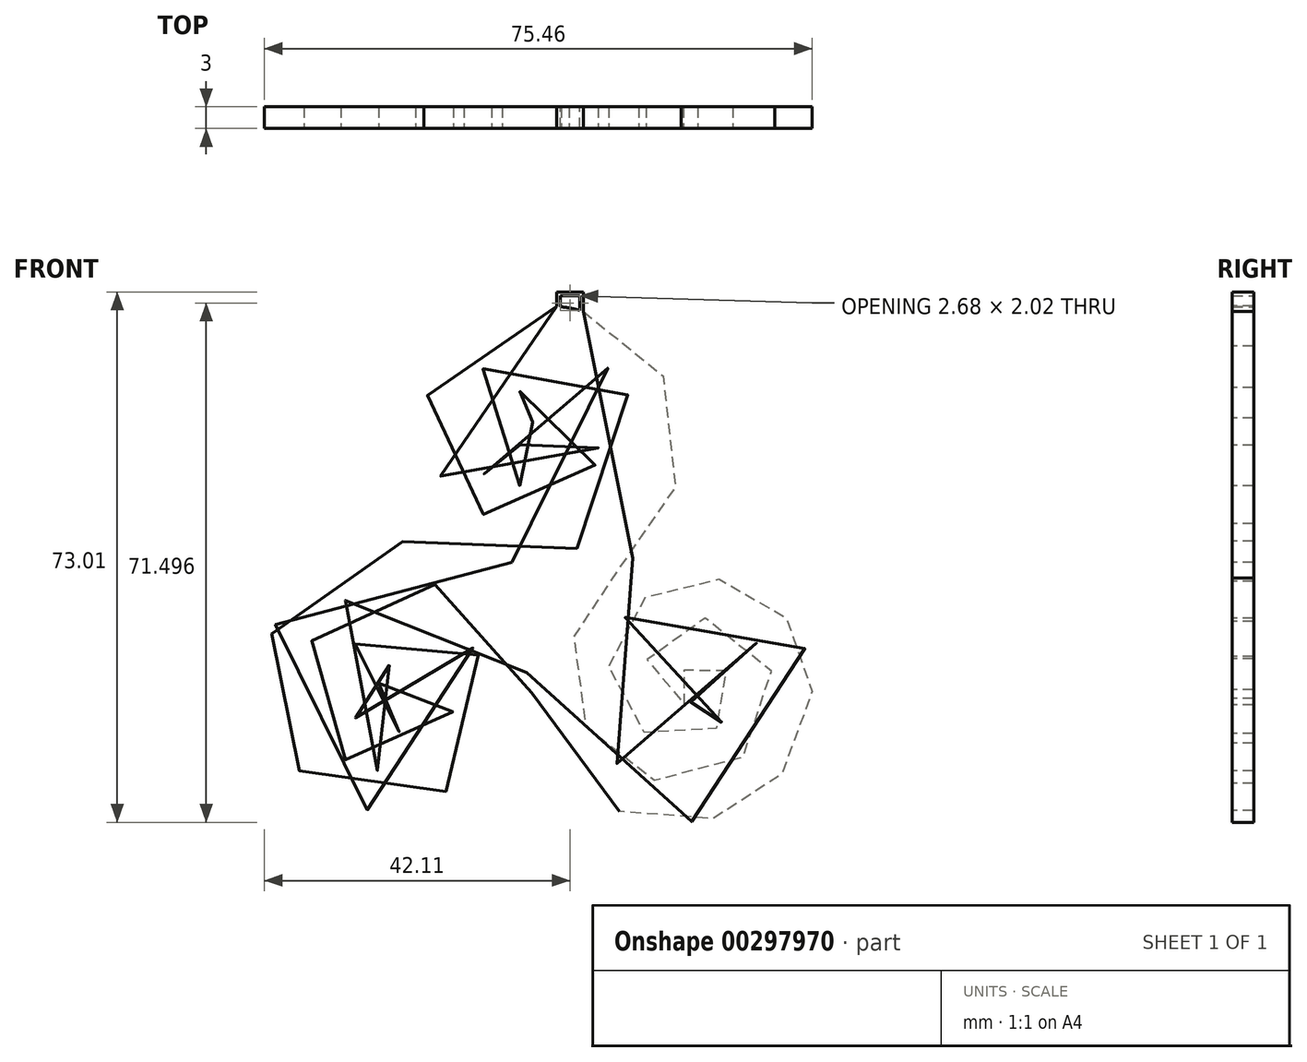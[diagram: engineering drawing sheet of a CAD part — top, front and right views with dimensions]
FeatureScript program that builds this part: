
annotation { "Feature Type Name" : "Feature", "Feature Type Description" : "" }
export const myFeature = defineFeature(function(context is Context, id is Id, definition is map)
    precondition{}
    {
        {
            var Q0;
            Q0=qCreatedBy(makeId("Front.planeOp"),FACE);
            var sketch = newSketch(context, id + "F0", { "sketchPlane" : qUnion([Q0])});
            skFitSpline(sketch, "E0", {"points": [v(-58.42, 20.36) * mm, v(-57.04, 18.98) * mm, v(-57.56, 15.52) * mm, v(-61.88, 14.48) * mm, v(-65.86, 17.42) * mm, v(-67.08, 21.06) * mm, v(-65, 26.77) * mm, v(-58.94, 29.7) * mm, v(-53.06, 28.84) * mm, v(-48.9, 26.07) * mm, v(-46.48, 20.36) * mm, v(-47.34, 12.05) * mm, v(-51.84, 6.86) * mm, v(-59.11, 3.92) * mm, v(-67.77, 4.96) * mm, v(-73.3, 9.8) * mm, v(-76.6, 15) * mm, v(-77.63, 21.4) * mm, v(-76.42, 28.5) * mm, v(-71.4, 35.6) * mm, v(-62.92, 39.92) * mm, v(-55.65, 40.61) * mm, v(-45.44, 38.02) * mm, v(-35.57, 39.4) * mm, v(-29.52, 43.9) * mm, v(-26.05, 53.42) * mm, v(-29.34, 63.64) * mm, v(-37.65, 67.62) * mm, v(-45.79, 65.89) * mm, v(-49.25, 61.73) * mm, v(-49.77, 53.94) * mm, v(-45.1, 48.75) * mm, v(-38.69, 49.79) * mm, v(-36.79, 53.77) * mm, v(-38.34, 56.89) * mm, v(-39.04, 57.75) * mm, v(-40.77, 57.06) * mm, v(-41.29, 54.8) * mm, v(-43.54, 54.12) * mm, v(-44.75, 56.37) * mm, v(-44.23, 60.17) * mm, v(-40.42, 61.9) * mm, v(-35.75, 61.21) * mm, v(-32.11, 57.06) * mm, v(-32.11, 51.17) * mm, v(-35.23, 46.33) * mm, v(-40.07, 43.38) * mm, v(-46.3, 44.08) * mm, v(-50.98, 46.67) * mm, v(-54.27, 51.52) * mm, v(-55.65, 57.4) * mm, v(-52.36, 66.92) * mm, v(-44.75, 71.94) * mm, v(-37.65, 73.16) * mm, v(-29.17, 70.39) * mm, v(-21.9, 61.9) * mm, v(-20.69, 49.62) * mm, v(-26.05, 39.23) * mm, v(-31.6, 34.56) * mm, v(-34.54, 29.2) * mm, v(-35.57, 21.57) * mm, v(-32.28, 13.61) * mm, v(-26.92, 8.94) * mm, v(-17.75, 7.73) * mm, v(-10.82, 12.05) * mm, v(-7.36, 19.67) * mm, v(-10.65, 27.63) * mm, v(-17.05, 30.23) * mm, v(-21.9, 28.33) * mm, v(-25.02, 24) * mm, v(-23.46, 20.02) * mm, v(-20, 18.29) * mm, v(-17.92, 19.84) * mm, v(-19.3, 21.57) * mm, v(-19.88, 22.63) * mm, v(-18.82, 24.57) * mm, v(-16.87, 24.86) * mm, v(-14.06, 23.11) * mm, v(-13.08, 20.1) * mm, v(-14.54, 16.02) * mm, v(-18.52, 13.2) * mm, v(-24.55, 14.08) * mm, v(-28.82, 18.06) * mm, v(-30.18, 23.8) * mm, v(-28.43, 29.62) * mm, v(-23.48, 34.19) * mm, v(-17.94, 35.74) * mm, v(-12.5, 34.97) * mm, v(-7.35, 31.95) * mm, v(-3.37, 26.42) * mm, v(-2.2, 20.88) * mm, v(-3.27, 13.3) * mm, v(-7.94, 7.09) * mm, v(-12.8, 3.5) * mm, v(-21.92, 2.13) * mm, v(-29.5, 3.98) * mm, v(-34.94, 8.06) * mm, v(-38.92, 13.3) * mm, v(-41.26, 21.75) * mm, v(-44.95, 29.53) * mm, v(-50.87, 33.7) * mm, v(-55.25, 35.06) * mm, v(-60.4, 35.16) * mm, v(-66.61, 32.54) * mm, v(-71.57, 26.03) * mm, v(-72.15, 20.88) * mm, v(-71.18, 16.02) * mm, v(-67.3, 11.26) * mm, v(-61.85, 9.22) * mm, v(-55.44, 10.49) * mm, v(-52.23, 14.86) * mm, v(-52.04, 20.98) * mm, v(-55.44, 24.09) * mm, v(-58.94, 24.47) * mm, v(-61.85, 21.85) * mm, v(-60.98, 19.33) * mm, v(-59.9, 19.33) * mm, v(-58.42, 20.36) * mm]});
            skSolve(sketch);
        }
        {
            var Q0;
            Q0=makeQuery(id+"F0.imprint","IMPRINT",FACE,{"disambiguationData":[TD([[makeQuery(id+"F0.imprint","IMPRINT",EDGE,{"derivedFrom":sQuery(id+"F0.wireOp",EDGE,"E0")}),-1.0]])]});
            extrude(context, id + "F1", {"entities" : qUnion([Q0]), "depth" : 3 * mm});
        }
        {
            var Q0;
            Q0=qCreatedBy(makeId("Front.planeOp"),FACE);
            var sketch = newSketch(context, id + "F2", { "sketchPlane" : qUnion([Q0])});
            skLineSegment(sketch, "E1", {"start": v(-37.36, 73.07) * mm, "end": v(-37.36, 75.12) * mm});
            skLineSegment(sketch, "E2", {"start": v(-37.36, 75.12) * mm, "end": v(-33.68, 75.12) * mm});
            skLineSegment(sketch, "E3", {"start": v(-33.68, 75.12) * mm, "end": v(-33.68, 72.12) * mm});
            skLineSegment(sketch, "E4", {"start": v(-37.36, 73.07) * mm, "end": v(-36.86, 73.07) * mm});
            skLineSegment(sketch, "E5", {"start": v(-36.86, 73.07) * mm, "end": v(-36.86, 74.62) * mm});
            skLineSegment(sketch, "E6", {"start": v(-36.86, 74.62) * mm, "end": v(-34.18, 74.62) * mm});
            skLineSegment(sketch, "E7", {"start": v(-34.18, 74.62) * mm, "end": v(-34.18, 72.15) * mm});
            skLineSegment(sketch, "E8", {"start": v(-34.18, 72.15) * mm, "end": v(-33.68, 72.12) * mm});
            skSolve(sketch);
        }
        {
            var Q0;
            Q0=makeQuery(id+"F2.imprint","IMPRINT",FACE,{"disambiguationData":[TD([[makeQuery(id+"F2.imprint","IMPRINT",EDGE,{"derivedFrom":sQuery(id+"F2.wireOp",EDGE,"E1")}),-1.0]])]});
            extrude(context, id + "F3", {"entities" : qUnion([Q0]), "operationType" : NewBodyOperationType.ADD, "depth" : 3 * mm});
        }
    });
